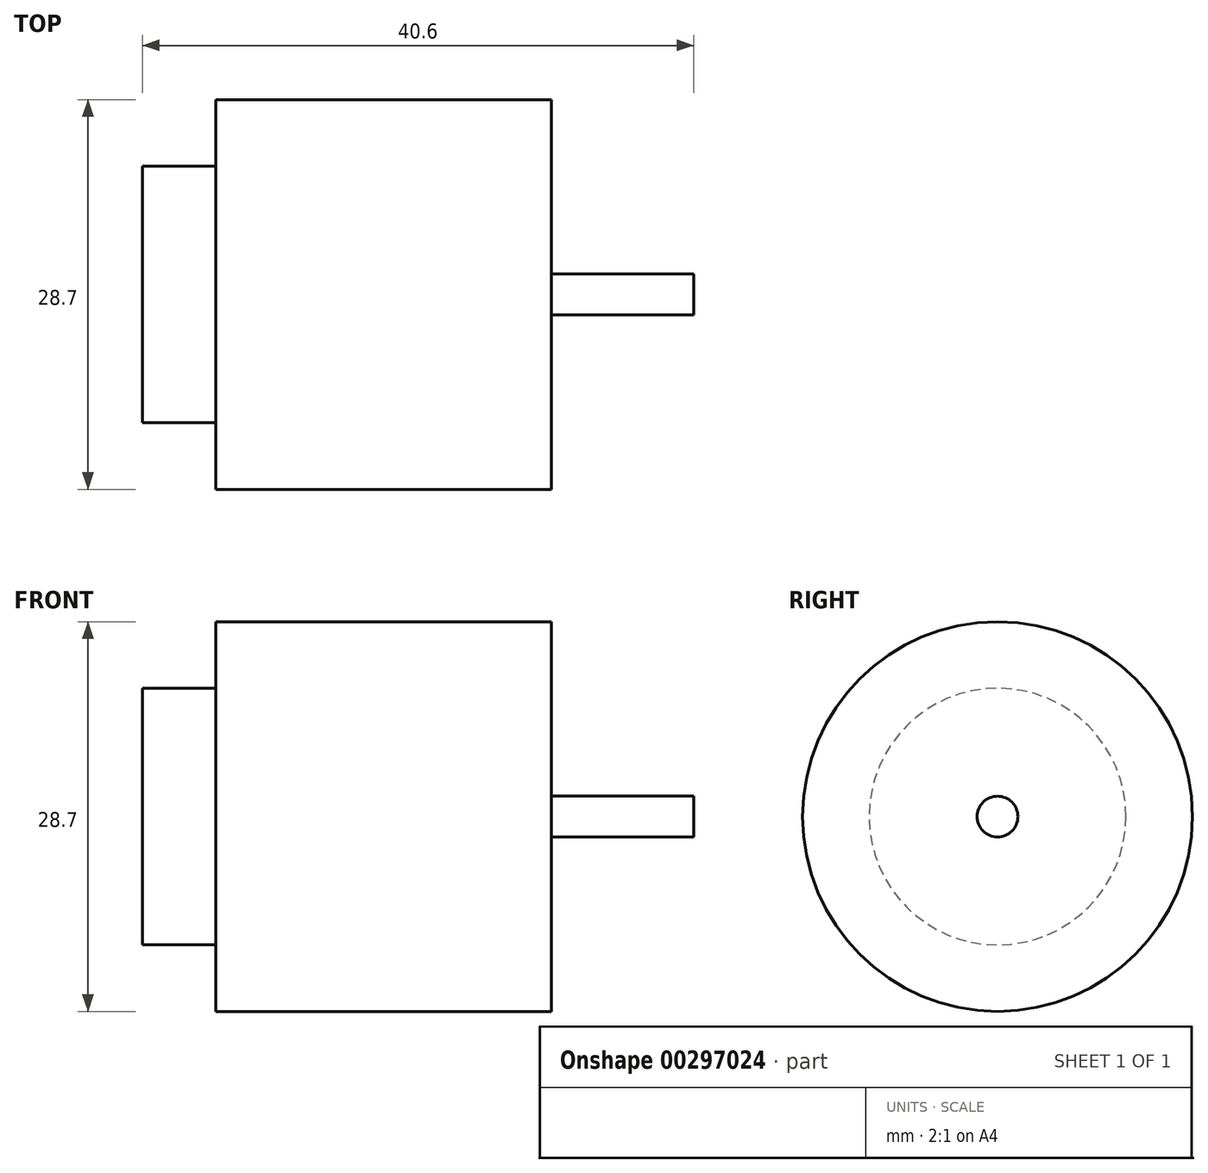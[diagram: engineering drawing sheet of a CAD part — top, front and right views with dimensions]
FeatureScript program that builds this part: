
annotation { "Feature Type Name" : "Feature", "Feature Type Description" : "" }
export const myFeature = defineFeature(function(context is Context, id is Id, definition is map)
    precondition{}
    {
        {
            var Q0;
            Q0=qCreatedBy(makeId("Front.planeOp"),FACE);
            var sketch = newSketch(context, id + "F0", { "sketchPlane" : qUnion([Q0])});
            skLineSegment(sketch, "E0.bottom", {"start": v(-24.7, 14.35) * mm, "end": v(0, 14.35) * mm});
            skLineSegment(sketch, "E0.top", {"start": v(-24.7, -14.35) * mm, "end": v(0, -14.35) * mm});
            skLineSegment(sketch, "E0.left", {"start": v(-24.7, 14.35) * mm, "end": v(-24.7, -14.35) * mm});
            skLineSegment(sketch, "E0.right", {"start": v(0, 14.35) * mm, "end": v(0, -14.35) * mm});
            skLineSegment(sketch, "E1.bottom", {"start": v(-30.1, -9.45) * mm, "end": v(-24.7, -9.45) * mm});
            skLineSegment(sketch, "E1.top", {"start": v(-30.1, 9.45) * mm, "end": v(-24.7, 9.45) * mm});
            skLineSegment(sketch, "E1.left", {"start": v(-30.1, 9.45) * mm, "end": v(-30.1, -9.45) * mm});
            skLineSegment(sketch, "E1.right", {"start": v(-24.7, 9.45) * mm, "end": v(-24.7, -9.45) * mm});
            skLineSegment(sketch, "E2", {"start": v(0, 0) * mm, "end": v(-30.1, 0) * mm});
            skLineSegment(sketch, "E3.bottom", {"start": v(0, -1.5) * mm, "end": v(10.5, -1.5) * mm});
            skLineSegment(sketch, "E3.top", {"start": v(0, 1.5) * mm, "end": v(10.5, 1.5) * mm});
            skLineSegment(sketch, "E3.left", {"start": v(0, 1.5) * mm, "end": v(0, -1.5) * mm});
            skLineSegment(sketch, "E3.right", {"start": v(10.5, 1.5) * mm, "end": v(10.5, -1.5) * mm});
            skLineSegment(sketch, "E4", {"start": v(0, 0) * mm, "end": v(10.5, 0) * mm});
            skSolve(sketch);
        }
        {
            var Q0;
            {var subQ0=sQuery(id+"F0.wireOp",EDGE,"E1.top");Q0=makeQuery(id+"F0.imprint","IMPRINT",FACE,{"disambiguationData":[TD([[makeQuery(id+"F0.imprint","IMPRINT",EDGE,{"derivedFrom":subQ0}),-1.0]])]});}
            var Q1;
            {var subQ1=sQuery(id+"F0.wireOp",EDGE,"E0.bottom");Q1=makeQuery(id+"F0.imprint","IMPRINT",FACE,{"disambiguationData":[TD([[makeQuery(id+"F0.imprint","IMPRINT",EDGE,{"derivedFrom":subQ1}),-1.0]])]});}
            var Q2;
            {var subQ0=sQuery(id+"F0.wireOp",EDGE,"E3.top");Q2=makeQuery(id+"F0.imprint","IMPRINT",FACE,{"disambiguationData":[TD([[makeQuery(id+"F0.imprint","IMPRINT",EDGE,{"derivedFrom":subQ0}),-1.0]])]});}
            var Q3;
            Q3=sQuery(id+"F0.wireOp",EDGE,"E2");
            revolve(context, id + "F1", {"entities" : qUnion([Q0, Q1, Q2]), "axis" : qUnion([Q3]), "revolveType" : RevolveType.FULL});
        }
    });
